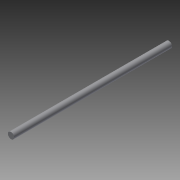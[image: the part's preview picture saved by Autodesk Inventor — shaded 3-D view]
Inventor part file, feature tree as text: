
AUTODESK INVENTOR PART (.ipt)
format: ipt  version: 2014 (Build 180170000, 170)  size: 65,024 bytes
history: native  units: mm
features: extrude x1, sketch x1
ambient origin geometry x8: Origin, YZ Plane, XZ Plane, XY Plane, X Axis, Y Axis, Z Axis, Center Point
bodies: Solid1 (feature_tree)
feature tree (2):
  extrude  "Extrusion1"  Depth=125.0mm TaperAngle=0.0deg
  sketch  "Sketch1"  dims[d0=5.0mm d1=125.0mm d2=0.0mm]
